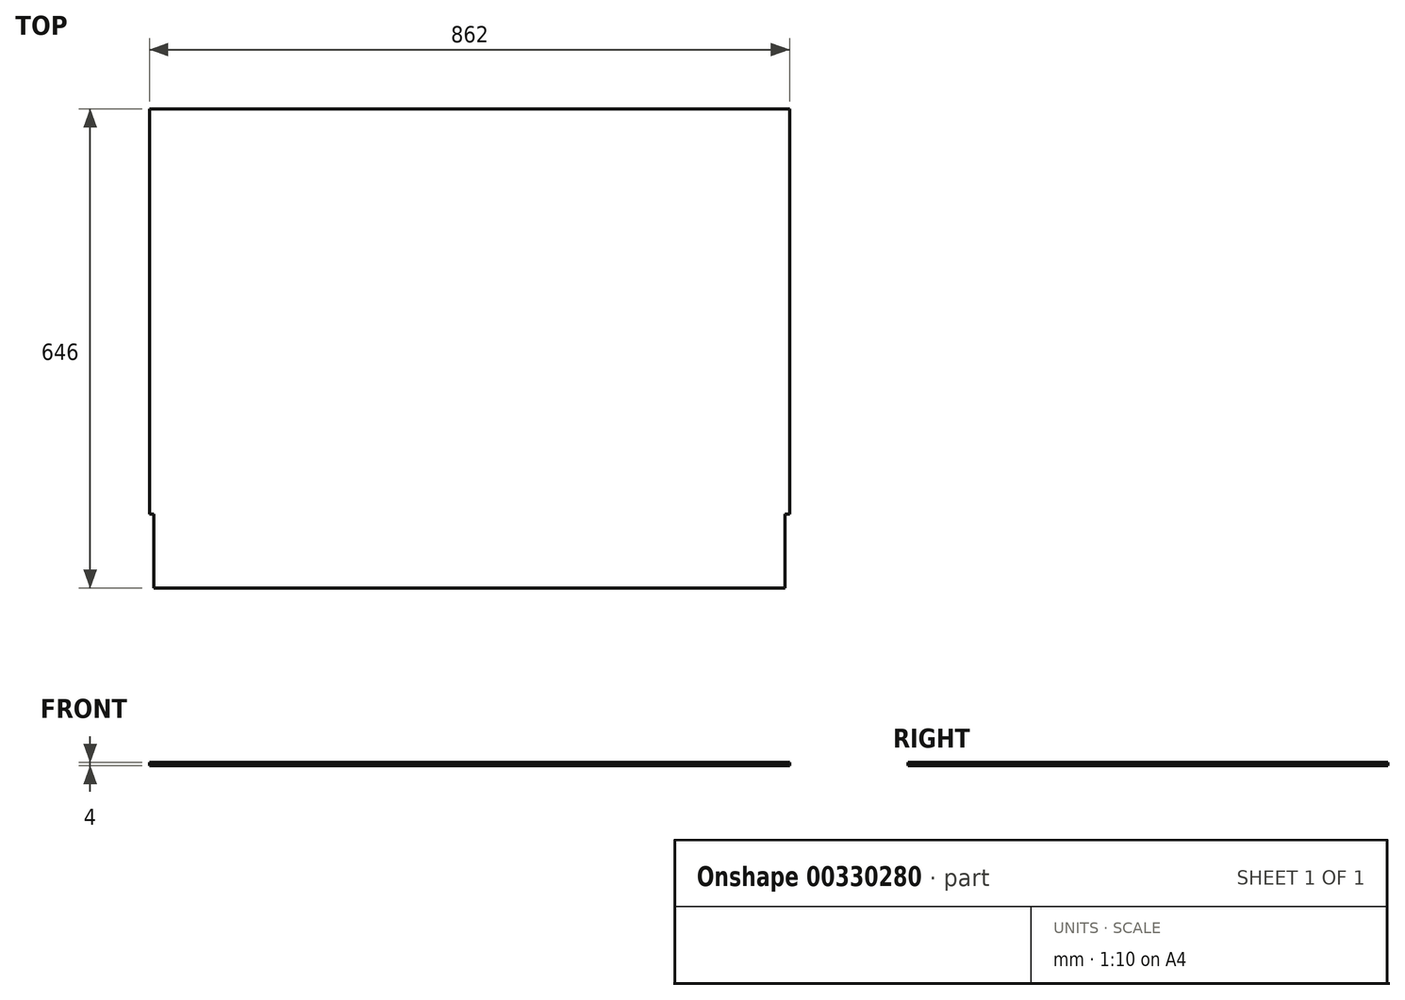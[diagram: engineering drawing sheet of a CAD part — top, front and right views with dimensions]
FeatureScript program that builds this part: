
annotation { "Feature Type Name" : "Feature", "Feature Type Description" : "" }
export const myFeature = defineFeature(function(context is Context, id is Id, definition is map)
    precondition{}
    {
        {
            var Q0;
            Q0=qCreatedBy(makeId("Top.planeOp"),FACE);
            var sketch = newSketch(context, id + "F0", { "sketchPlane" : qUnion([Q0])});
            skLineSegment(sketch, "E0.bottom", {"start": v(0, 0) * mm, "end": v(862, 0) * mm});
            skLineSegment(sketch, "E0.top", {"start": v(0, 646) * mm, "end": v(862, 646) * mm});
            skLineSegment(sketch, "E0.left", {"start": v(0, 0) * mm, "end": v(0, 646) * mm});
            skLineSegment(sketch, "E0.right", {"start": v(862, 0) * mm, "end": v(862, 646) * mm});
            skSolve(sketch);
        }
        {
            var Q0;
            Q0 = qSketchRegion(id + "F0", true);
            extrude(context, id + "F1", {"entities" : qUnion([Q0]), "depth" : 4 * mm});
        }
        {
            var Q0;
            Q0=makeQuery(id+"F1.opExtrude","CAP_FACE",FACE,{"disambiguationData":[OSD([sQuery(id+"F0.wireOp",EDGE,"E0.bottom"),sQuery(id+"F0.wireOp",EDGE,"E0.top"),sQuery(id+"F0.wireOp",EDGE,"E0.left"),sQuery(id+"F0.wireOp",EDGE,"E0.right")])],"isStart":false});
            var sketch = newSketch(context, id + "F2", { "sketchPlane" : qUnion([Q0])});
            skLineSegment(sketch, "E1.bottom", {"start": v(0, 0) * mm, "end": v(6, 0) * mm});
            skLineSegment(sketch, "E1.top", {"start": v(0, 100) * mm, "end": v(6, 100) * mm});
            skLineSegment(sketch, "E1.left", {"start": v(0, 0) * mm, "end": v(0, 100) * mm});
            skLineSegment(sketch, "E1.right", {"start": v(6, 0) * mm, "end": v(6, 100) * mm});
            skLineSegment(sketch, "E2.bottom", {"start": v(862, 0) * mm, "end": v(856, 0) * mm});
            skLineSegment(sketch, "E2.top", {"start": v(862, 100) * mm, "end": v(856, 100) * mm});
            skLineSegment(sketch, "E2.left", {"start": v(862, 0) * mm, "end": v(862, 100) * mm});
            skLineSegment(sketch, "E2.right", {"start": v(856, 0) * mm, "end": v(856, 100) * mm});
            skSolve(sketch);
        }
        {
            var Q0;
            Q0 = qSketchRegion(id + "F2", true);
            extrude(context, id + "F3", {"entities" : qUnion([Q0]), "operationType" : NewBodyOperationType.REMOVE, "oppositeDirection" : true, "depth" : 329 * mm});
        }
    });
